# Revit family: 0067953 Sylvania Lighting Fixture START Waterproof Single 1200 IP65 EM 2800lm 840
name_source: partatom
category: Lighting Fixtures
revit_build: Autodesk Revit 2016 (Build: 20150220_1215(x64)
units: mm (PartAtom-declared; Revit-internal decimal feet)

## family parameters
Cut with Voids When Loaded = No
Host = Face
Light Source = Yes
OmniClass Number = 23.80.70.11.14
OmniClass Title = General Luminaries, Directional
Part Type = Normal
Room Calculation Point = No
Round Connector Dimension = Use Diameter
Shared = No

## types (2) — shared parameters
AccessoryMaterial = Diffuser-Sylvania-Glow
Apparent Load = 24 VA
Assembly Code = D5020200
AssetType = Fixed
BodyMaterial = Body-Sylvania-Gray
ClassificationName = Uniclass2015
ClassificationValue = EF_70_80
Color Filter = 16777215
Default Elevation = 1219 mm
DiffuserMaterial = Diffuser-Sylvania-Transparent
Dimming Lamp Color Temperature Shift = <None>
DocumentationLiterature = http://www.sylvania-lighting.com
DurationUnit = hours
ElectricShockClassification = Class I
Emit Shape Visible in Rendering = No
Emit from Rectangle Length = 1252 mm  [stored 4.10761 ft]
Emit from Rectangle Width = 64 mm  [stored 0.209974 ft]
ExpectedLife = 50000
IfcExportAs = IfcLightFixtureType
IfcExportType = IfcLightFixtureType
ImpactProtectionIndex = IK08
IngressProtection = IP65
Keynote = 16500
Lamp = LED
LampColourRenderingIndex = 80
LampColourTemperature = 4000 K
LampsType = LED
Length = 1272 mm  [stored 4.17323 ft]
Manufacturer = Feilo Sylvania
ManufacturerName = Feilo Sylvania
Material = polycarbonate housing, polycarbonate diffuser
Model = START Waterproof Single 1200 IP65 EM 2800lm 840
ModelNumber = 0067953
ModelReference = START Waterproof Single 1200 IP65 EM 2800lm 840
Name = START Waterproof Single 1200 IP65 EM 2800lm 840
NominalHeight = 75 mm
NominalLength = 1278 mm  [stored 4.19291 ft]
PowerConsumption = 24 W
ReflectorMaterial = <By Category>
Tilt Angle = -90.00°
Type Image = <None>
TypeName = START Waterproof Single 1200 IP65 EM 2800lm 840
URL = http://www.sylvania-lighting.com
Voltage = 0 V
Width = 84 mm  [stored 0.275591 ft]
zero-valued in all types: Cost, NominalWidth, PowerFactor

## per-type parameters (varying)
| type | LampNominalLuminous | LuminousEfficacy | Photometric Web File |
| 0067953 ST WTRPRF S 1200 IP65 EM 2800LM 840 | 2750 lm | 115 lm/W | 0067953.ies |
| 0067953 ST WTRPRF S 1200 IP65 EM 2800LM 840 Emergency mode | 234 lm | 9.761 lm/W | 0067953EM.ies |

note: [stored X ft] marks values corroborated as IEEE doubles in the binary element streams (Revit-internal decimal feet)

## geometry (parser evidence)
native form markers: Sweep x4
no freeform markers — native parametric forms only
